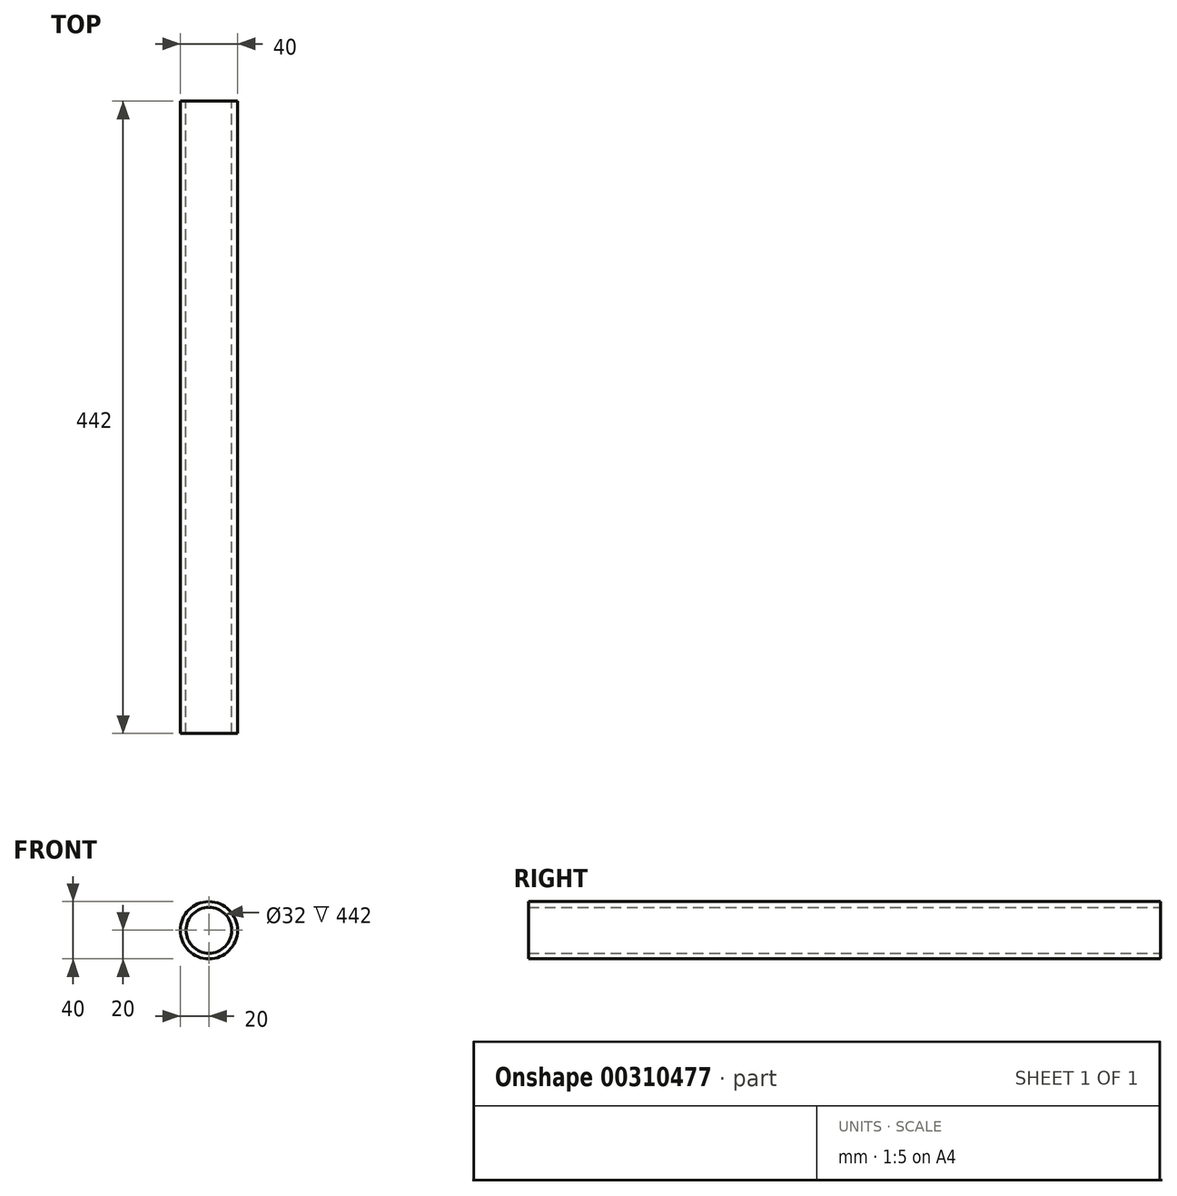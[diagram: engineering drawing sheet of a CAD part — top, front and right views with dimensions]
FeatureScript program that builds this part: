
annotation { "Feature Type Name" : "Feature", "Feature Type Description" : "" }
export const myFeature = defineFeature(function(context is Context, id is Id, definition is map)
    precondition{}
    {
        {
            var Q0;
            Q0=qCreatedBy(makeId("Front.planeOp"),FACE);
            var sketch = newSketch(context, id + "F0", { "sketchPlane" : qUnion([Q0])});
            skCircle(sketch, "E0", {"center": v(0, 0) * mm, "radius": 20 * mm});
            skCircle(sketch, "E1.0", {"center": v(0, 0) * mm, "radius": 16 * mm});
            skSolve(sketch);
        }
        {
            var Q0;
            Q0=makeQuery(id+"F0.imprint","IMPRINT",FACE,{"disambiguationData":[TD([[makeQuery(id+"F0.imprint","IMPRINT",EDGE,{"derivedFrom":sQuery(id+"F0.wireOp",EDGE,"E0")}),1.0]])]});
            extrude(context, id + "F1", {"entities" : qUnion([Q0]), "depth" : 442 * mm});
        }
    });
